# Revit family: HVAC_Boilers_Enertech_CTC-Accumulator-Tank_2-500
name_source: partatom
category: Specialty Equipment
revit_build: Autodesk Revit 2018 (Build: 20190510_1515(x64)
units: mm (PartAtom-declared; Revit-internal decimal feet)

## family parameters
Always vertical = No
Cut with Voids When Loaded = No
OmniClass Number = 23.75.00.00
OmniClass Title = Climate Control (HVAC)
Part Type = Normal
Room Calculation Point = No
Round Connector Dimension = Use Diameter
Shared = No
Work Plane-Based = No

## types (1)
- CTC Ackumulatortank 2 500
    AssetType = Fixed
    BIMObjectName = HVAC_Boilers_Enertech_CTC-Accumulator-Tank_2-500
    Brand = CTC
    Category = Storage tank, hot water
    Color = Grey
    Cost = 0 $
    Description = CTC Hot water storage tanks is a series of  coil/storage tanks suitable for DHW-preparation and hot water storage, availiable in two models and five sizes. CTC Hot Water Storage Tank 1:  coil tanks for efficient DHW heating. CTC Hot Water Storage Tank 2: volume tanks for hot water storage.
    DurationUnit = Year
    EANNumber = 7333077097622
    ElectricalDeviceNominalPower = 0 W
    HasProtectiveEarth = Yes
    IfcExportAs = IfcElectricalDeviceCommon
    IfcExportType = HEATER
    Manufacturer = Enertech AB
    ManufacturerCountry = Sweden
    ManufacturerName = Enertech AB
    ManufacturerURL = https://ctc.se
    Material = Steel
    MaxOperatingPressureThermalStore = 6 bar
    MaxOperatingTemperature = 100 °C
    MinimumCeilingHeight = 1890 mm
    Model = CTC Ackumulatortank 2 500
    ModelNumber = 589903001
    NBSDescription = Air to water heat pumps
    NBSReference = 90-40-40/320
    Name = CTC-Accumulator-Tank_2-500
    NominalCurrent = 0 A
    NominalDepth = 840 mm  [stored 2.75591 ft]
    NominalFrequencyRange = 0 Hz
    NominalHeight = 1780 mm  [stored 5.8399 ft]
    NominalVoltage = 0 V
    NominalWidth = 840 mm  [stored 2.75591 ft]
    NumberOfPoles = 1
    PhaseAngle = 0.00°
    PowerFactor = 0 W
    ProductInformation = CTC Hot water storage tanks is a series of  coil/storage tanks suitable for DHW-preparation and hot water storage, availiable in two models and five sizes. CTC Hot Water Storage Tank 1:  coil tanks for efficient DHW heating. CTC Hot Water Storage Tank 2: volume tanks for hot water storage.
    PumpMainMaterial = Stainless Steel
    RatedCurrent = 0 A
    RatedVoltage = 0 V
    Shape = Round
    Size = Ø840x1780 mm
    Standby heat loss, Storage tank = 104 W
    Touchscreen = no
    UNSPSCCode = 24111810
    URL = https://ctc-heating.com
    Uniclass2 = Pr_40_70_65
    Uniclass2015Description = Preparation catering equipment
    Uniclass2015Reference = Pr_40_70_65
    UsageCurrent = 0 A
    Version = 1
    VersionDate = 24/08/2021
    WarrantyDurationUnit = Year
    WaterVolumeHeathingSystem = 503 l
    Weight = 118 kg

note: [stored X ft] marks values corroborated as IEEE doubles in the binary element streams (Revit-internal decimal feet)

## geometry (parser evidence)
native form markers: Sweep x4
no freeform markers — native parametric forms only
